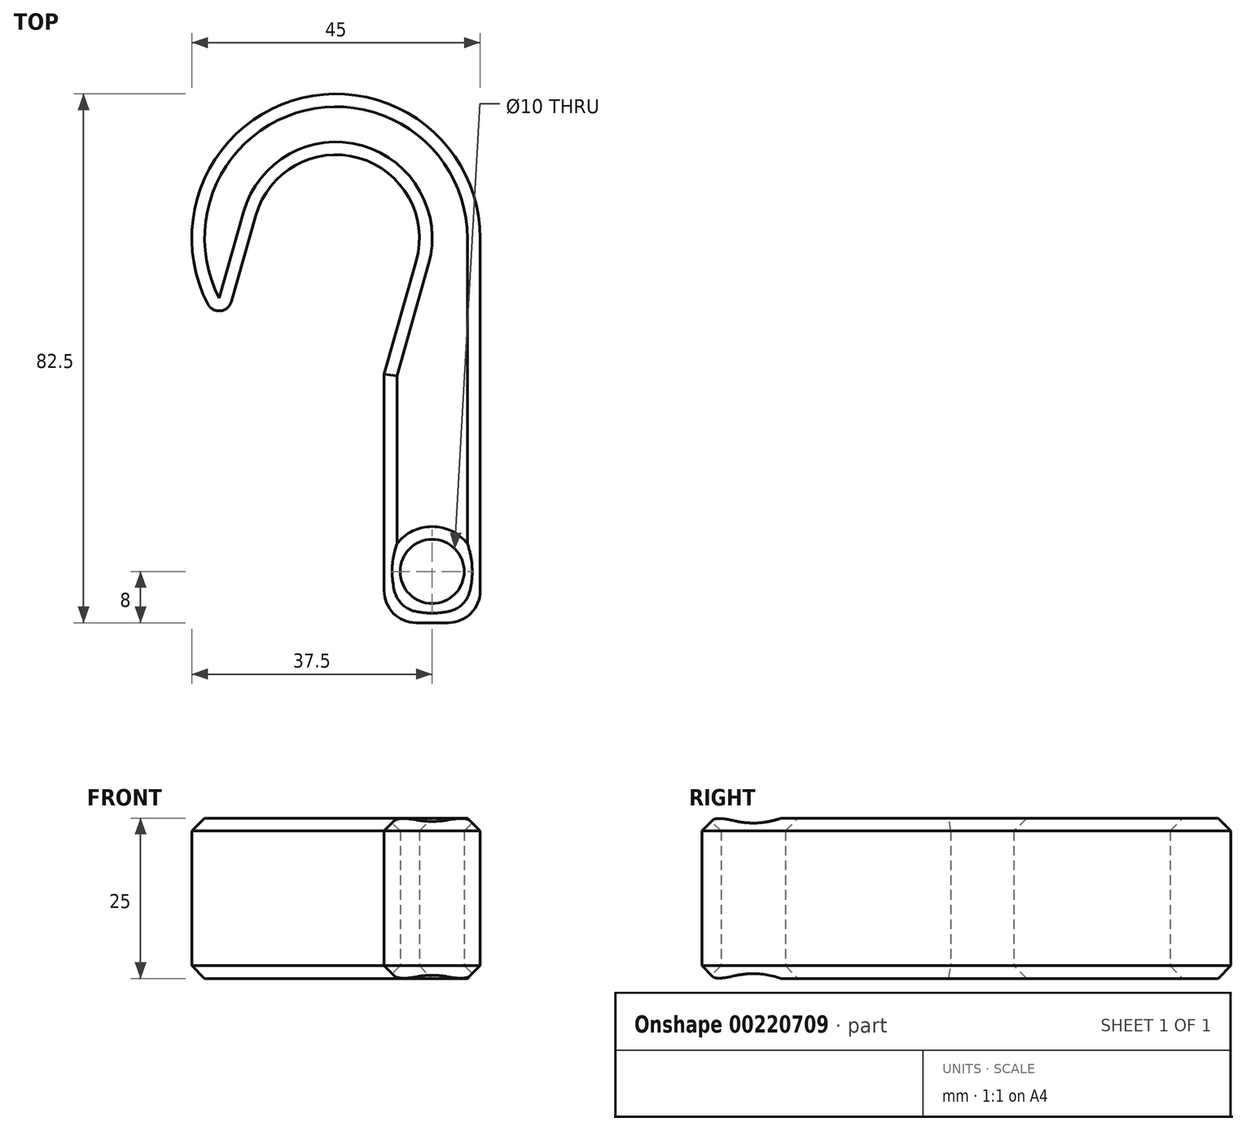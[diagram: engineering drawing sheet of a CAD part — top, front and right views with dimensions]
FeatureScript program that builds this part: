
annotation { "Feature Type Name" : "Feature", "Feature Type Description" : "" }
export const myFeature = defineFeature(function(context is Context, id is Id, definition is map)
    precondition{}
    {
        {
            var Q0;
            Q0=qCreatedBy(makeId("Top.planeOp"),FACE);
            var sketch = newSketch(context, id + "F0", { "sketchPlane" : qUnion([Q0])});
            skCircle(sketch, "E0", {"center": v(0, 0) * mm, "radius": 22.5 * mm});
            skCircle(sketch, "E1", {"center": v(0, 0) * mm, "radius": 13 * mm});
            skLineSegment(sketch, "E2", {"start": v(22.5, 0) * mm, "end": v(22.5, -60) * mm});
            skLineSegment(sketch, "E3", {"start": v(22.5, -60) * mm, "end": v(7.5, -60) * mm});
            skLineSegment(sketch, "E4", {"start": v(7.5, -60) * mm, "end": v(7.5, -21.21) * mm});
            skLineSegment(sketch, "E5", {"start": v(7.5, -21.21) * mm, "end": v(12.5, -3.54) * mm});
            skLineSegment(sketch, "E6", {"start": v(-12.5, 3.54) * mm, "end": v(-17.51, -14.12) * mm});
            skCircle(sketch, "E7", {"center": v(15, -52) * mm, "radius": 5 * mm});
            skPoint(sketch, "E7.centerSnap0", {"position": v(15, -60) * mm});
            skSolve(sketch);
        }
        {
            var Q0;
            {var subQ0=sQuery(id+"F0.wireOp",EDGE,"E5");Q0=makeQuery(id+"F0.imprint","IMPRINT",FACE,{"disambiguationData":[TD([[makeQuery(id+"F0.imprint","IMPRINT",EDGE,{"derivedFrom":subQ0}),-1.0]])]});}
            var Q1;
            {var subQ1=sQuery(id+"F0.wireOp",EDGE,"E2");Q1=makeQuery(id+"F0.imprint","IMPRINT",FACE,{"disambiguationData":[TD([[makeQuery(id+"F0.imprint","IMPRINT",EDGE,{"derivedFrom":subQ1}),-1.0]])]});}
            extrude(context, id + "F1", {"entities" : qUnion([Q0, Q1]), "depth" : 25 * mm});
        }
        {
            var Q0;
            Q0=makeQuery(id+"F1.opExtrude","SWEPT_EDGE",EDGE,{"disambiguationData":[OSD([sQuery(id+"F0.wireOp",EDGE,"E2"),sQuery(id+"F0.wireOp",EDGE,"E3")])]});
            var Q1;
            Q1=makeQuery(id+"F1.opExtrude","SWEPT_EDGE",EDGE,{"disambiguationData":[OSD([sQuery(id+"F0.wireOp",EDGE,"E3"),sQuery(id+"F0.wireOp",EDGE,"E4")])]});
            fillet(context, id + "F2", {"entities" : qUnion([Q0, Q1]), "radius" : 5 * mm, "tangentPropagation" : true, "allowEdgeOverflow" : false});
        }
        {
            var Q0;
            Q0=makeQuery(id+"F1.opExtrude","SWEPT_EDGE",EDGE,{"disambiguationData":[OSD([sQuery(id+"F0.wireOp",EDGE,"E0"),sQuery(id+"F0.wireOp",EDGE,"E6")])]});
            fillet(context, id + "F3", {"entities" : qUnion([Q0]), "radius" : 2 * mm, "tangentPropagation" : true, "allowEdgeOverflow" : false});
        }
        {
            var Q0;
            Q0=makeQuery(id+"F1.opExtrude","CAP_FACE",FACE,{"disambiguationData":[OSD([sQuery(id+"F0.wireOp",EDGE,"E0"),sQuery(id+"F0.wireOp",EDGE,"E1"),sQuery(id+"F0.wireOp",EDGE,"E2"),sQuery(id+"F0.wireOp",EDGE,"E3"),sQuery(id+"F0.wireOp",EDGE,"E4"),sQuery(id+"F0.wireOp",EDGE,"E5"),sQuery(id+"F0.wireOp",EDGE,"E6"),sQuery(id+"F0.wireOp",EDGE,"E7")])],"isStart":false});
            var Q1;
            Q1=makeQuery(id+"F1.opExtrude","CAP_FACE",FACE,{"disambiguationData":[OSD([sQuery(id+"F0.wireOp",EDGE,"E0"),sQuery(id+"F0.wireOp",EDGE,"E1"),sQuery(id+"F0.wireOp",EDGE,"E2"),sQuery(id+"F0.wireOp",EDGE,"E3"),sQuery(id+"F0.wireOp",EDGE,"E4"),sQuery(id+"F0.wireOp",EDGE,"E5"),sQuery(id+"F0.wireOp",EDGE,"E6"),sQuery(id+"F0.wireOp",EDGE,"E7")])],"isStart":true});
            chamfer(context, id + "F4", {"entities" : qUnion([Q0, Q1]), "width" : 2 * mm, "tangentPropagation" : true});
        }
    });
